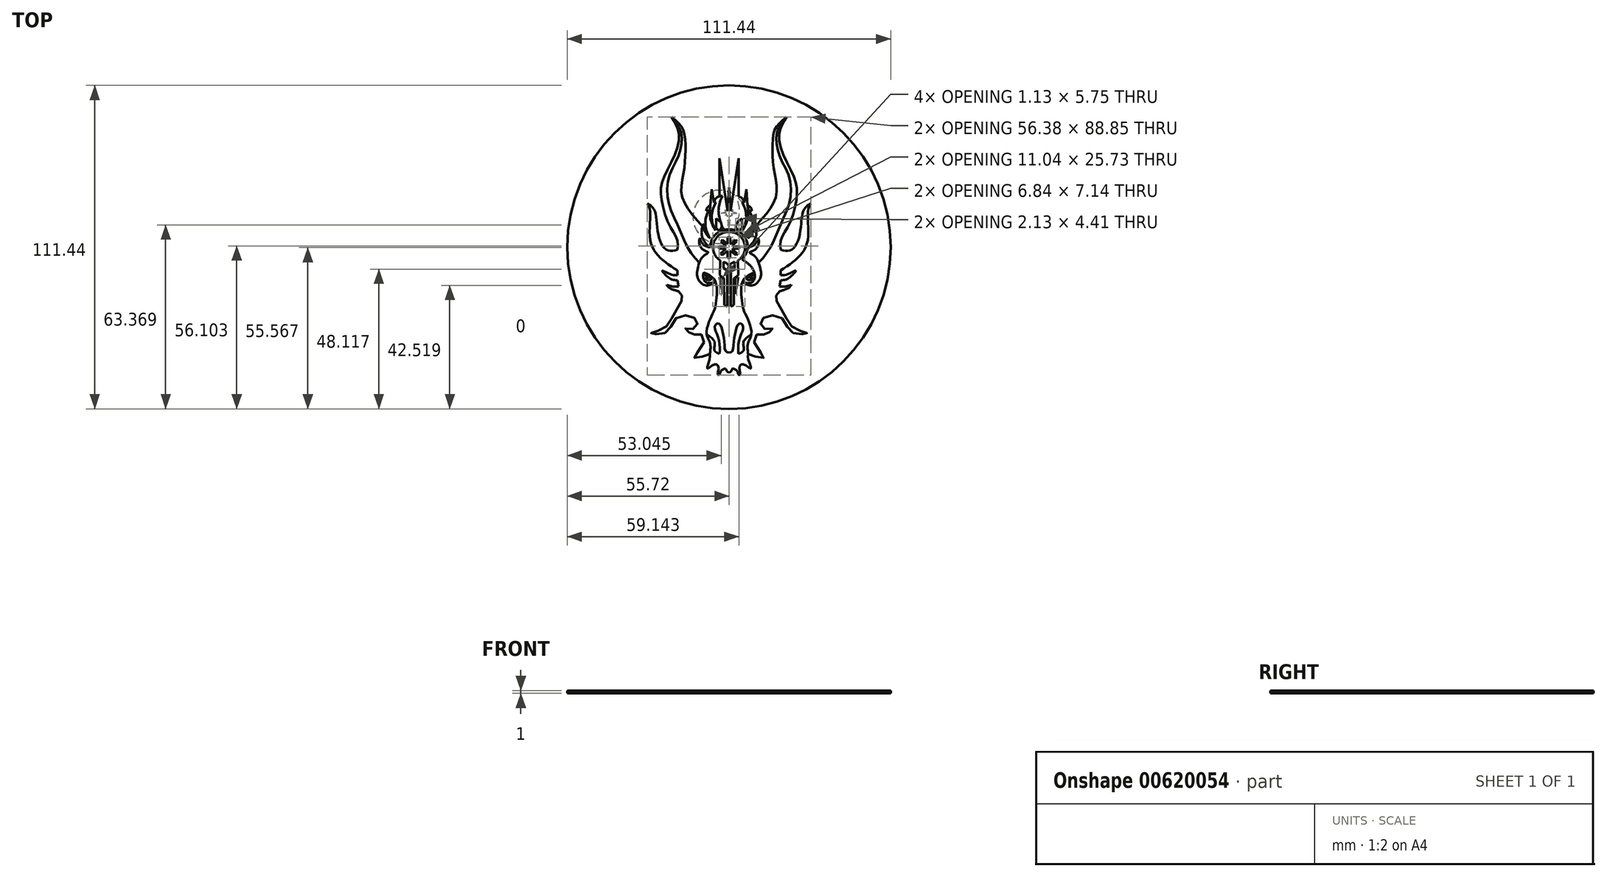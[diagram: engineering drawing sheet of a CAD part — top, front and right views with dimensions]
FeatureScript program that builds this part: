
annotation { "Feature Type Name" : "Feature", "Feature Type Description" : "" }
export const myFeature = defineFeature(function(context is Context, id is Id, definition is map)
    precondition{}
    {
        {
            var Q0;
            Q0=qCreatedBy(makeId("Top.planeOp"),FACE);
            var sketch = newSketch(context, id + "F0", { "sketchPlane" : qUnion([Q0])});
            skLineSegment(sketch, "E0", {"start": v(0.64, -20.47) * mm, "end": v(1.63, -19.96) * mm});
            skLineSegment(sketch, "E1", {"start": v(1.63, -19.96) * mm, "end": v(1.73, -10.73) * mm});
            skLineSegment(sketch, "E2", {"start": v(1.73, -10.73) * mm, "end": v(3.14, -9.62) * mm});
            skLineSegment(sketch, "E3", {"start": v(0.64, -20.47) * mm, "end": v(0.64, -8.04) * mm});
            skLineSegment(sketch, "E4", {"start": v(0.64, -8.04) * mm, "end": v(1.91, -7.17) * mm});
            skLineSegment(sketch, "E5", {"start": v(1.91, -7.17) * mm, "end": v(1.91, -5.13) * mm});
            skArc(sketch, "E6", {"start": v(0, -5.41) * mm, "mid": v(5.52, -0.08) * mm, "end": v(0, 5.26) * mm});
            skLineSegment(sketch, "E7", {"start": v(3.14, -9.62) * mm, "end": v(3.08, -4.56) * mm});
            skLineSegment(sketch, "E8", {"start": v(2.78, 8.47) * mm, "end": v(4.49, 9.86) * mm});
            skLineSegment(sketch, "E9", {"start": v(4.49, 9.86) * mm, "end": v(4.49, 6.67) * mm});
            skLineSegment(sketch, "E10", {"start": v(4.49, 6.67) * mm, "end": v(3.26, 5.44) * mm});
            skLineSegment(sketch, "E11", {"start": v(3.26, 5.44) * mm, "end": v(2.36, 7.04) * mm});
            skArc(sketch, "E12", {"start": v(2.78, 8.47) * mm, "mid": v(3.6, 13.1) * mm, "end": v(2.25, 17.62) * mm});
            skArc(sketch, "E13", {"start": v(1.4, 5.97) * mm, "mid": v(1.94, 6.45) * mm, "end": v(2.36, 7.04) * mm});
            skArc(sketch, "E14", {"start": v(5.2, 15.4) * mm, "mid": v(4.16, 17.1) * mm, "end": v(2.25, 17.62) * mm});
            skArc(sketch, "E15", {"start": v(4.66, 5.73) * mm, "mid": v(5.95, 10.6) * mm, "end": v(4.49, 15.4) * mm});
            skArc(sketch, "E16", {"start": v(4.66, 5.73) * mm, "mid": v(6.4, 9.87) * mm, "end": v(6.4, 14.36) * mm});
            skArc(sketch, "E17", {"start": v(7.87, 12.55) * mm, "mid": v(7.4, 13.67) * mm, "end": v(6.4, 14.36) * mm});
            skArc(sketch, "E18", {"start": v(6.4, 3.03) * mm, "mid": v(8.15, 7.7) * mm, "end": v(7.02, 12.55) * mm});
            skArc(sketch, "E19", {"start": v(6.4, 3.03) * mm, "mid": v(8.24, 5.24) * mm, "end": v(8.72, 8.06) * mm});
            skArc(sketch, "E20", {"start": v(6.4, 0) * mm, "mid": v(9.22, 3.55) * mm, "end": v(8.72, 8.06) * mm});
            skArc(sketch, "E21", {"start": v(6.4, 0) * mm, "mid": v(8.83, 0.88) * mm, "end": v(10, 3.17) * mm});
            skArc(sketch, "E22", {"start": v(7.87, -1.4) * mm, "mid": v(9.96, 0.4) * mm, "end": v(10, 3.17) * mm});
            skArc(sketch, "E23", {"start": v(4.4, -4.17) * mm, "mid": v(6.17, 1.87) * mm, "end": v(1.4, 5.97) * mm});
            skLineSegment(sketch, "E24", {"start": v(2.11, -11.19) * mm, "end": v(3.24, -10.33) * mm});
            skLineSegment(sketch, "E25", {"start": v(3.24, -10.33) * mm, "end": v(2.13, -16.08) * mm});
            skLineSegment(sketch, "E26", {"start": v(2.13, -16.08) * mm, "end": v(2.11, -11.19) * mm});
            skFitSpline(sketch, "E27", {"points": [v(4.4, -4.17) * mm, v(7.37, -6.41) * mm, v(8.7, -8.69) * mm, v(8.8, -10.78) * mm, v(7.79, -12.14) * mm, v(5.83, -12.33) * mm, v(4.9, -12.1) * mm], "startDerivative": vector(14.8, -9.52) * mm, "endDerivative": vector(-7.08, 2.25) * mm});
            skFitSpline(sketch, "E28", {"points": [v(4.9, -12.1) * mm, v(6.3, -12.93) * mm, v(8.86, -12.9) * mm, v(10.92, -10.27) * mm, v(10.85, -7.7) * mm, v(8.96, -3.16) * mm, v(7.15, -1.86) * mm, v(7.87, -1.4) * mm], "startDerivative": vector(10.53, -7.87) * mm, "endDerivative": vector(13.03, 5.28) * mm});
            skLineSegment(sketch, "E29", {"start": v(0, 6.49) * mm, "end": v(0.53, 10.42) * mm});
            skLineSegment(sketch, "E30", {"start": v(0.53, 10.42) * mm, "end": v(0.53, 10.9) * mm});
            skLineSegment(sketch, "E31", {"start": v(0.53, 10.9) * mm, "end": v(1.11, 10.9) * mm});
            skLineSegment(sketch, "E32", {"start": v(1.11, 10.9) * mm, "end": v(0.9, 11.5) * mm});
            skLineSegment(sketch, "E33", {"start": v(0.9, 11.5) * mm, "end": v(2.65, 11.74) * mm});
            skLineSegment(sketch, "E34", {"start": v(2.65, 11.74) * mm, "end": v(1.05, 12.22) * mm});
            skLineSegment(sketch, "E35", {"start": v(1.05, 12.22) * mm, "end": v(1.43, 12.9) * mm});
            skLineSegment(sketch, "E36", {"start": v(1.43, 12.9) * mm, "end": v(0.54, 12.51) * mm});
            skLineSegment(sketch, "E37", {"start": v(4.49, 15.4) * mm, "end": v(5.2, 15.4) * mm});
            skLineSegment(sketch, "E38", {"start": v(7.02, 12.55) * mm, "end": v(7.87, 12.55) * mm});
            skLineSegment(sketch, "E39", {"start": v(0.54, 12.51) * mm, "end": v(0, 20.62) * mm});
            skFitSpline(sketch, "E40", {"points": [v(9.1, 7.21) * mm, v(11.57, 9.94) * mm, v(16.22, 17.62) * mm, v(15.5, 26.76) * mm, v(15.04, 35.45) * mm, v(16.05, 41.02) * mm, v(19.84, 44.8) * mm], "startDerivative": vector(17.57, 18.84) * mm, "endDerivative": vector(30.07, 23.23) * mm});
            skFitSpline(sketch, "E41", {"points": [v(19.84, 44.8) * mm, v(17.95, 41.4) * mm, v(17.57, 35.2) * mm, v(22.5, 23.82) * mm, v(23.38, 17.62) * mm, v(20.86, 8.06) * mm, v(17.95, 2.86) * mm, v(17.82, -0.94) * mm], "startDerivative": vector(-19, -28.92) * mm, "endDerivative": vector(3.8, -35.47) * mm});
            skFitSpline(sketch, "E42", {"points": [v(17.82, -0.94) * mm, v(21.49, -0.94) * mm, v(24.4, 4.5) * mm, v(25.66, 12.55) * mm, v(28.2, 15) * mm], "startDerivative": vector(18.53, -4.1) * mm, "endDerivative": vector(14.4, 8.9) * mm});
            skFitSpline(sketch, "E43", {"points": [v(28.2, 15) * mm, v(27.2, 12.55) * mm, v(27.2, 2.86) * mm, v(23.9, -3.47) * mm, v(17.82, -8.02) * mm], "startDerivative": vector(-7.89, -11.91) * mm, "endDerivative": vector(-24.05, -15.72) * mm});
            skFitSpline(sketch, "E44", {"points": [v(17.82, -9.6) * mm, v(19.84, -9.45) * mm, v(22.97, -8.12) * mm, v(22.2, -9.26) * mm, v(19.84, -11.05) * mm, v(17.82, -11.4) * mm], "startDerivative": vector(9, -1.2) * mm, "endDerivative": vector(-10.69, -0.53) * mm});
            skFitSpline(sketch, "E45", {"points": [v(17.41, -13.6) * mm, v(19.43, -13.54) * mm, v(21.5, -12.99) * mm], "startDerivative": vector(4.1, -0.14) * mm, "endDerivative": vector(4.08, 1.35) * mm});
            skFitSpline(sketch, "E46", {"points": [v(21.5, -12.99) * mm, v(20.47, -14.08) * mm, v(17.41, -15.2) * mm], "startDerivative": vector(-2.04, -2.86) * mm, "endDerivative": vector(-5.9, -1.63) * mm});
            skFitSpline(sketch, "E47", {"points": [v(16.22, -16.63) * mm, v(16.22, -18.21) * mm, v(18.81, -22.8) * mm, v(21.5, -27.16) * mm, v(25.66, -29.19) * mm, v(26.89, -29.7) * mm, v(24.1, -29.98) * mm, v(20.72, -28.5) * mm, v(17.82, -24.1) * mm, v(12.47, -24.07) * mm, v(10.92, -26.03) * mm, v(11.97, -28.05) * mm, v(15, -28.05) * mm, v(14.24, -29.07) * mm, v(12.4, -30.05) * mm, v(9.88, -29.98) * mm, v(8.72, -32.93) * mm, v(12.12, -37.94) * mm, v(10.06, -37.94) * mm, v(6.57, -36.87) * mm], "startDerivative": vector(-7.73, -38) * mm, "endDerivative": vector(-58.93, 20.62) * mm});
            skFitSpline(sketch, "E48", {"points": [v(6.57, -36.87) * mm, v(6.77, -39.08) * mm, v(7.5, -41.8) * mm, v(5.91, -40.84) * mm, v(4.27, -40.38) * mm, v(3.57, -41.53) * mm, v(3.81, -42.88) * mm, v(3.8, -43.99) * mm, v(3.3, -43.97) * mm, v(2.93, -42.88) * mm, v(1.9, -41.98) * mm, v(1.1, -41.87) * mm, v(0.8, -42.7) * mm, v(0, -43.12) * mm], "startDerivative": vector(-1, -19.1) * mm, "endDerivative": vector(-15.31, -4.03) * mm});
            skFitSpline(sketch, "E49", {"points": [v(6.57, -36.87) * mm, v(6.57, -32.93) * mm, v(7.68, -30.03) * mm, v(6.57, -24.92) * mm, v(4.96, -21.32) * mm, v(4.27, -16.76) * mm, v(4.9, -11.39) * mm, v(8.7, -8.69) * mm], "startDerivative": vector(-3.54, 31.13) * mm, "endDerivative": vector(30.9, 14.24) * mm});
            skFitSpline(sketch, "E50", {"points": [v(10.23, -5.36) * mm, v(13.96, -0.61) * mm, v(17.95, 8.06) * mm, v(20.86, 15.59) * mm, v(20.86, 23.82) * mm, v(17.95, 30.25) * mm, v(16.39, 35.89) * mm, v(16.74, 40.18) * mm, v(19.84, 44.8) * mm], "startDerivative": vector(32.67, 35.42) * mm, "endDerivative": vector(33.02, 40.5) * mm});
            skFitSpline(sketch, "E51", {"points": [v(7.68, -30.03) * mm, v(4.9, -32.93) * mm, v(4.9, -35.74) * mm, v(0.8, -37.26) * mm, v(0, -37.26) * mm], "startDerivative": vector(-12.98, -8.92) * mm, "endDerivative": vector(-4.07, 0.48) * mm});
            skFitSpline(sketch, "E52", {"points": [v(3.24, -36.75) * mm, v(3.24, -33.56) * mm, v(4.27, -29.61) * mm, v(4.9, -27.84) * mm, v(4.27, -26.36) * mm, v(3.24, -26.54) * mm, v(2.25, -28.96) * mm, v(1.63, -32.93) * mm, v(1.1, -35.89) * mm, v(0, -36.33) * mm], "startDerivative": vector(-1.6, 23.43) * mm, "endDerivative": vector(-16.16, -2.15) * mm});
            skFitSpline(sketch, "E53", {"points": [v(6.16, -11.09) * mm, v(6.95, -10.16) * mm, v(8.89, -9.7) * mm, v(8.2, -10.97) * mm, v(6.16, -11.09) * mm]});
            skFitSpline(sketch, "E54", {"points": [v(6.95, -10.16) * mm, v(8.2, -10.97) * mm, v(7.93, -10.45) * mm, v(6.95, -10.16) * mm]});
            skLineSegment(sketch, "E55", {"start": v(0.54, 12.51) * mm, "end": v(3.34, 30.61) * mm});
            skLineSegment(sketch, "E56", {"start": v(3.34, 30.61) * mm, "end": v(3.34, 17.51) * mm});
            skLineSegment(sketch, "E57", {"start": v(5.2, 15.4) * mm, "end": v(5.93, 19.97) * mm});
            skLineSegment(sketch, "E58", {"start": v(5.93, 19.97) * mm, "end": v(6.4, 14.36) * mm});
            skLineSegment(sketch, "E59", {"start": v(8.72, 8.06) * mm, "end": v(8.72, 12.11) * mm});
            skArc(sketch, "E60", {"start": v(0.43, -1.43) * mm, "mid": v(0.55, -1.39) * mm, "end": v(0.66, -1.33) * mm});
            skLineSegment(sketch, "E61", {"start": v(0, 3.42) * mm, "end": v(0.45, 3.42) * mm});
            skLineSegment(sketch, "E62", {"start": v(0.45, 3.42) * mm, "end": v(0.45, 1.24) * mm});
            skLineSegment(sketch, "E63", {"start": v(0.68, 1.13) * mm, "end": v(2.25, 2.52) * mm});
            skLineSegment(sketch, "E64", {"start": v(2.25, 2.52) * mm, "end": v(2.74, 1.96) * mm});
            skLineSegment(sketch, "E65", {"start": v(2.74, 1.96) * mm, "end": v(1.2, 0.62) * mm});
            skLineSegment(sketch, "E66", {"start": v(0, -3.72) * mm, "end": v(0.43, -3.72) * mm});
            skLineSegment(sketch, "E67", {"start": v(0.43, -3.72) * mm, "end": v(0.43, -1.43) * mm});
            skLineSegment(sketch, "E68", {"start": v(0.66, -1.33) * mm, "end": v(2.38, -2.74) * mm});
            skLineSegment(sketch, "E69", {"start": v(2.38, -2.74) * mm, "end": v(2.86, -2.15) * mm});
            skLineSegment(sketch, "E70", {"start": v(2.86, -2.15) * mm, "end": v(1.2, -0.8) * mm});
            skLineSegment(sketch, "E71", {"start": v(1.33, -0.52) * mm, "end": v(3.42, -0.52) * mm});
            skLineSegment(sketch, "E72", {"start": v(3.42, -0.52) * mm, "end": v(3.42, 0.24) * mm});
            skLineSegment(sketch, "E73", {"start": v(3.42, 0.24) * mm, "end": v(1.36, 0.24) * mm});
            skArc(sketch, "E74.trimOffspring", {"start": v(1.36, 0.24) * mm, "mid": v(1.3, 0.44) * mm, "end": v(1.2, 0.62) * mm});
            skArc(sketch, "E75.trimOffspring", {"start": v(0.68, 1.13) * mm, "mid": v(0.57, 1.2) * mm, "end": v(0.45, 1.24) * mm});
            skArc(sketch, "E76.trimOffspring", {"start": v(1.2, -0.8) * mm, "mid": v(1.28, -0.66) * mm, "end": v(1.33, -0.52) * mm});
            skPoint(sketch, "E77.orphan", {"position": v(0, -1.5) * mm});
            skPoint(sketch, "E78.orphan", {"position": v(0, 1.32) * mm});
            skLineSegment(sketch, "E79", {"start": v(16.22, -16.63) * mm, "end": v(17.41, -15.2) * mm});
            skLineSegment(sketch, "E80", {"start": v(17.82, -11.4) * mm, "end": v(17.41, -13.6) * mm});
            skLineSegment(sketch, "E81", {"start": v(17.82, -8.02) * mm, "end": v(17.82, -9.6) * mm});
            skArc(sketch, "E82.MirrorCS", {"start": v(-0.68, 1.13) * mm, "mid": v(-0.57, 1.2) * mm, "end": v(-0.45, 1.24) * mm});
            skLineSegment(sketch, "E83.MirrorCS", {"start": v(-1.33, -0.52) * mm, "end": v(-3.42, -0.52) * mm});
            skArc(sketch, "E84.MirrorCS", {"start": v(-1.36, 0.24) * mm, "mid": v(-1.3, 0.44) * mm, "end": v(-1.2, 0.62) * mm});
            skLineSegment(sketch, "E85.MirrorCS", {"start": v(-0.68, 1.13) * mm, "end": v(-2.25, 2.52) * mm});
            skLineSegment(sketch, "E86.MirrorCS", {"start": v(0, -3.72) * mm, "end": v(-0.43, -3.72) * mm});
            skLineSegment(sketch, "E87.MirrorCS", {"start": v(0, 3.42) * mm, "end": v(-0.45, 3.42) * mm});
            skLineSegment(sketch, "E88.MirrorCS", {"start": v(-2.38, -2.74) * mm, "end": v(-2.86, -2.15) * mm});
            skLineSegment(sketch, "E89.MirrorCS", {"start": v(-0.66, -1.33) * mm, "end": v(-2.38, -2.74) * mm});
            skLineSegment(sketch, "E90.MirrorCS", {"start": v(-3.42, -0.52) * mm, "end": v(-3.42, 0.24) * mm});
            skLineSegment(sketch, "E91.MirrorCS", {"start": v(-2.74, 1.96) * mm, "end": v(-1.2, 0.62) * mm});
            skLineSegment(sketch, "E92.MirrorCS", {"start": v(-2.25, 2.52) * mm, "end": v(-2.74, 1.96) * mm});
            skArc(sketch, "E93.MirrorCS", {"start": v(-1.2, -0.8) * mm, "mid": v(-1.28, -0.66) * mm, "end": v(-1.33, -0.52) * mm});
            skLineSegment(sketch, "E94.MirrorCS", {"start": v(-3.42, 0.24) * mm, "end": v(-1.36, 0.24) * mm});
            skLineSegment(sketch, "E95.MirrorCS", {"start": v(-2.86, -2.15) * mm, "end": v(-1.2, -0.8) * mm});
            skLineSegment(sketch, "E96.MirrorCS", {"start": v(-0.45, 3.42) * mm, "end": v(-0.45, 1.24) * mm});
            skLineSegment(sketch, "E97.MirrorCS", {"start": v(-0.43, -3.72) * mm, "end": v(-0.43, -1.43) * mm});
            skArc(sketch, "E98.MirrorCS", {"start": v(-0.43, -1.43) * mm, "mid": v(-0.55, -1.39) * mm, "end": v(-0.66, -1.33) * mm});
            skLineSegment(sketch, "E99.MirrorCS", {"start": v(-1.11, 10.9) * mm, "end": v(-0.9, 11.5) * mm});
            skLineSegment(sketch, "E100.MirrorCS", {"start": v(-0.53, 10.9) * mm, "end": v(-1.11, 10.9) * mm});
            skArc(sketch, "E101.MirrorCS", {"start": v(-1.4, 5.97) * mm, "mid": v(-1.94, 6.45) * mm, "end": v(-2.36, 7.04) * mm});
            skLineSegment(sketch, "E102.MirrorCS", {"start": v(-0.9, 11.5) * mm, "end": v(-2.65, 11.74) * mm});
            skLineSegment(sketch, "E103.MirrorCS", {"start": v(0, 6.49) * mm, "end": v(-0.53, 10.42) * mm});
            skLineSegment(sketch, "E104.MirrorCS", {"start": v(-3.26, 5.44) * mm, "end": v(-2.36, 7.04) * mm});
            skLineSegment(sketch, "E105.MirrorCS", {"start": v(-4.49, 6.67) * mm, "end": v(-3.26, 5.44) * mm});
            skLineSegment(sketch, "E106.MirrorCS", {"start": v(-1.05, 12.22) * mm, "end": v(-1.43, 12.9) * mm});
            skLineSegment(sketch, "E107.MirrorCS", {"start": v(-4.49, 15.4) * mm, "end": v(-5.2, 15.4) * mm});
            skLineSegment(sketch, "E108.MirrorCS", {"start": v(-7.02, 12.55) * mm, "end": v(-7.87, 12.55) * mm});
            skLineSegment(sketch, "E109.MirrorCS", {"start": v(-0.53, 10.42) * mm, "end": v(-0.53, 10.9) * mm});
            skArc(sketch, "E110.MirrorCS", {"start": v(0, -5.41) * mm, "mid": v(-5.52, -0.08) * mm, "end": v(0, 5.26) * mm});
            skLineSegment(sketch, "E111.MirrorCS", {"start": v(-2.78, 8.47) * mm, "end": v(-4.49, 9.86) * mm});
            skLineSegment(sketch, "E112.MirrorCS", {"start": v(-4.49, 9.86) * mm, "end": v(-4.49, 6.67) * mm});
            skLineSegment(sketch, "E113.MirrorCS", {"start": v(-2.65, 11.74) * mm, "end": v(-1.05, 12.22) * mm});
            skArc(sketch, "E114.MirrorCS", {"start": v(-7.87, 12.55) * mm, "mid": v(-7.4, 13.67) * mm, "end": v(-6.4, 14.36) * mm});
            skArc(sketch, "E115.MirrorCS", {"start": v(-4.66, 5.73) * mm, "mid": v(-6.4, 9.87) * mm, "end": v(-6.4, 14.36) * mm});
            skArc(sketch, "E116.MirrorCS", {"start": v(-6.4, 3.03) * mm, "mid": v(-8.24, 5.24) * mm, "end": v(-8.72, 8.06) * mm});
            skArc(sketch, "E117.MirrorCS", {"start": v(-4.4, -4.17) * mm, "mid": v(-6.17, 1.87) * mm, "end": v(-1.4, 5.97) * mm});
            skFitSpline(sketch, "E118.MirrorCS", {"points": [v(-17.41, -13.6) * mm, v(-19.43, -13.54) * mm, v(-21.5, -12.99) * mm], "startDerivative": vector(-4.1, -0.14) * mm, "endDerivative": vector(-4.08, 1.35) * mm});
            skArc(sketch, "E119.MirrorCS", {"start": v(-4.66, 5.73) * mm, "mid": v(-5.95, 10.6) * mm, "end": v(-4.49, 15.4) * mm});
            skLineSegment(sketch, "E120.MirrorCS", {"start": v(-1.43, 12.9) * mm, "end": v(-0.54, 12.51) * mm});
            skLineSegment(sketch, "E121.MirrorCS", {"start": v(-2.11, -11.19) * mm, "end": v(-3.24, -10.33) * mm});
            skFitSpline(sketch, "E122.MirrorCS", {"points": [v(-4.4, -4.17) * mm, v(-7.37, -6.41) * mm, v(-8.7, -8.69) * mm, v(-8.8, -10.78) * mm, v(-7.79, -12.14) * mm, v(-5.83, -12.33) * mm, v(-4.9, -12.1) * mm], "startDerivative": vector(-14.8, -9.52) * mm, "endDerivative": vector(7.08, 2.25) * mm});
            skLineSegment(sketch, "E123.MirrorCS", {"start": v(-17.82, -8.02) * mm, "end": v(-17.82, -9.6) * mm});
            skLineSegment(sketch, "E124.MirrorCS", {"start": v(-2.13, -16.08) * mm, "end": v(-2.11, -11.19) * mm});
            skLineSegment(sketch, "E125.MirrorCS", {"start": v(-5.2, 15.4) * mm, "end": v(-5.93, 19.97) * mm});
            skLineSegment(sketch, "E126.MirrorCS", {"start": v(-8.72, 8.06) * mm, "end": v(-8.72, 12.11) * mm});
            skFitSpline(sketch, "E127.MirrorCS", {"points": [v(-4.9, -12.1) * mm, v(-6.3, -12.93) * mm, v(-8.86, -12.9) * mm, v(-10.92, -10.27) * mm, v(-10.85, -7.7) * mm, v(-8.96, -3.16) * mm, v(-7.15, -1.86) * mm, v(-7.87, -1.4) * mm], "startDerivative": vector(-10.53, -7.87) * mm, "endDerivative": vector(-13.03, 5.28) * mm});
            skArc(sketch, "E128.MirrorCS", {"start": v(-7.87, -1.4) * mm, "mid": v(-9.96, 0.4) * mm, "end": v(-10, 3.17) * mm});
            skArc(sketch, "E129.MirrorCS", {"start": v(-6.4, 3.03) * mm, "mid": v(-8.15, 7.7) * mm, "end": v(-7.02, 12.55) * mm});
            skFitSpline(sketch, "E130.MirrorC", {"points": [v(-6.16, -11.09) * mm, v(-6.95, -10.16) * mm, v(-8.89, -9.7) * mm, v(-8.2, -10.97) * mm, v(-6.16, -11.09) * mm]});
            skFitSpline(sketch, "E131.MirrorC", {"points": [v(-6.95, -10.16) * mm, v(-8.2, -10.97) * mm, v(-7.93, -10.45) * mm, v(-6.95, -10.16) * mm]});
            skArc(sketch, "E132.MirrorCS", {"start": v(-6.4, 0) * mm, "mid": v(-9.22, 3.55) * mm, "end": v(-8.72, 8.06) * mm});
            skLineSegment(sketch, "E133.MirrorCS", {"start": v(-17.82, -11.4) * mm, "end": v(-17.41, -13.6) * mm});
            skFitSpline(sketch, "E134.MirrorCS", {"points": [v(-21.5, -12.99) * mm, v(-20.47, -14.08) * mm, v(-17.41, -15.2) * mm], "startDerivative": vector(2.04, -2.86) * mm, "endDerivative": vector(5.9, -1.63) * mm});
            skLineSegment(sketch, "E135.MirrorCS", {"start": v(-0.64, -20.47) * mm, "end": v(-1.63, -19.96) * mm});
            skLineSegment(sketch, "E136.MirrorCS", {"start": v(-1.73, -10.73) * mm, "end": v(-3.14, -9.62) * mm});
            skLineSegment(sketch, "E137.MirrorCS", {"start": v(-0.64, -8.04) * mm, "end": v(-1.91, -7.17) * mm});
            skArc(sketch, "E138.MirrorCS", {"start": v(-6.4, 0) * mm, "mid": v(-8.83, 0.88) * mm, "end": v(-10, 3.17) * mm});
            skLineSegment(sketch, "E139.MirrorCS", {"start": v(-1.91, -7.17) * mm, "end": v(-1.91, -5.13) * mm});
            skLineSegment(sketch, "E140.MirrorCS", {"start": v(-3.24, -10.33) * mm, "end": v(-2.13, -16.08) * mm});
            skLineSegment(sketch, "E141.MirrorCS", {"start": v(-3.14, -9.62) * mm, "end": v(-3.08, -4.56) * mm});
            skLineSegment(sketch, "E142.MirrorCS", {"start": v(-5.93, 19.97) * mm, "end": v(-6.4, 14.36) * mm});
            skArc(sketch, "E143.MirrorCS", {"start": v(-2.78, 8.47) * mm, "mid": v(-3.6, 13.1) * mm, "end": v(-2.25, 17.62) * mm});
            skLineSegment(sketch, "E144.MirrorCS", {"start": v(-16.22, -16.63) * mm, "end": v(-17.41, -15.2) * mm});
            skFitSpline(sketch, "E145.MirrorCS", {"points": [v(-17.82, -9.6) * mm, v(-19.84, -9.45) * mm, v(-22.97, -8.12) * mm, v(-22.2, -9.26) * mm, v(-19.84, -11.05) * mm, v(-17.82, -11.4) * mm], "startDerivative": vector(-9, -1.2) * mm, "endDerivative": vector(10.69, -0.53) * mm});
            skArc(sketch, "E146.MirrorCS", {"start": v(-5.2, 15.4) * mm, "mid": v(-4.16, 17.1) * mm, "end": v(-2.25, 17.62) * mm});
            skLineSegment(sketch, "E147.MirrorCS", {"start": v(-1.63, -19.96) * mm, "end": v(-1.73, -10.73) * mm});
            skLineSegment(sketch, "E148.MirrorCS", {"start": v(-0.64, -20.47) * mm, "end": v(-0.64, -8.04) * mm});
            skFitSpline(sketch, "E149.MirrorCS", {"points": [v(-7.68, -30.03) * mm, v(-4.9, -32.93) * mm, v(-4.9, -35.74) * mm, v(-0.8, -37.26) * mm, v(0, -37.26) * mm], "startDerivative": vector(12.98, -8.92) * mm, "endDerivative": vector(4.07, 0.48) * mm});
            skFitSpline(sketch, "E150.MirrorCS", {"points": [v(-3.24, -36.75) * mm, v(-3.24, -33.56) * mm, v(-4.27, -29.61) * mm, v(-4.9, -27.84) * mm, v(-4.27, -26.36) * mm, v(-3.24, -26.54) * mm, v(-2.25, -28.96) * mm, v(-1.63, -32.93) * mm, v(-1.1, -35.89) * mm, v(0, -36.33) * mm], "startDerivative": vector(1.6, 23.43) * mm, "endDerivative": vector(16.16, -2.15) * mm});
            skFitSpline(sketch, "E151.MirrorCS", {"points": [v(-6.57, -36.87) * mm, v(-6.77, -39.08) * mm, v(-7.5, -41.8) * mm, v(-5.91, -40.84) * mm, v(-4.27, -40.38) * mm, v(-3.57, -41.53) * mm, v(-3.81, -42.88) * mm, v(-3.8, -43.99) * mm, v(-3.3, -43.97) * mm, v(-2.93, -42.88) * mm, v(-1.9, -41.98) * mm, v(-1.1, -41.87) * mm, v(-0.8, -42.7) * mm, v(0, -43.12) * mm], "startDerivative": vector(1, -19.1) * mm, "endDerivative": vector(15.31, -4.03) * mm});
            skLineSegment(sketch, "E152.MirrorCS", {"start": v(-0.54, 12.51) * mm, "end": v(0, 20.62) * mm});
            skFitSpline(sketch, "E153.MirrorCS", {"points": [v(-6.57, -36.87) * mm, v(-6.57, -32.93) * mm, v(-7.68, -30.03) * mm, v(-6.57, -24.92) * mm, v(-4.96, -21.32) * mm, v(-4.27, -16.76) * mm, v(-4.9, -11.39) * mm, v(-8.7, -8.69) * mm], "startDerivative": vector(3.54, 31.13) * mm, "endDerivative": vector(-30.9, 14.24) * mm});
            skLineSegment(sketch, "E154.MirrorCS", {"start": v(-3.34, 30.61) * mm, "end": v(-3.34, 17.51) * mm});
            skLineSegment(sketch, "E155.MirrorCS", {"start": v(-0.54, 12.51) * mm, "end": v(-3.34, 30.61) * mm});
            skFitSpline(sketch, "E156.MirrorCS", {"points": [v(-17.82, -0.94) * mm, v(-21.49, -0.94) * mm, v(-24.4, 4.5) * mm, v(-25.66, 12.55) * mm, v(-28.2, 15) * mm], "startDerivative": vector(-18.53, -4.1) * mm, "endDerivative": vector(-14.4, 8.9) * mm});
            skFitSpline(sketch, "E157.MirrorCS", {"points": [v(-19.84, 44.8) * mm, v(-17.95, 41.4) * mm, v(-17.57, 35.2) * mm, v(-22.5, 23.82) * mm, v(-23.38, 17.62) * mm, v(-20.86, 8.06) * mm, v(-17.95, 2.86) * mm, v(-17.82, -0.94) * mm], "startDerivative": vector(19, -28.92) * mm, "endDerivative": vector(-3.8, -35.47) * mm});
            skFitSpline(sketch, "E158.MirrorCS", {"points": [v(-10.23, -5.36) * mm, v(-13.96, -0.61) * mm, v(-17.95, 8.06) * mm, v(-20.86, 15.59) * mm, v(-20.86, 23.82) * mm, v(-17.95, 30.25) * mm, v(-16.39, 35.89) * mm, v(-16.74, 40.18) * mm, v(-19.84, 44.8) * mm], "startDerivative": vector(-32.67, 35.42) * mm, "endDerivative": vector(-33.02, 40.5) * mm});
            skFitSpline(sketch, "E159.MirrorCS", {"points": [v(-28.2, 15) * mm, v(-27.2, 12.55) * mm, v(-27.2, 2.86) * mm, v(-23.9, -3.47) * mm, v(-17.82, -8.02) * mm], "startDerivative": vector(7.89, -11.91) * mm, "endDerivative": vector(24.05, -15.72) * mm});
            skFitSpline(sketch, "E160.MirrorCS", {"points": [v(-16.22, -16.63) * mm, v(-16.22, -18.21) * mm, v(-18.81, -22.8) * mm, v(-21.5, -27.16) * mm, v(-25.66, -29.19) * mm, v(-26.89, -29.7) * mm, v(-24.1, -29.98) * mm, v(-20.72, -28.5) * mm, v(-17.82, -24.1) * mm, v(-12.47, -24.07) * mm, v(-10.92, -26.03) * mm, v(-11.97, -28.05) * mm, v(-15, -28.05) * mm, v(-14.24, -29.07) * mm, v(-12.4, -30.05) * mm, v(-9.88, -29.98) * mm, v(-8.72, -32.93) * mm, v(-12.12, -37.94) * mm, v(-10.06, -37.94) * mm, v(-6.57, -36.87) * mm], "startDerivative": vector(7.73, -38) * mm, "endDerivative": vector(58.93, 20.62) * mm});
            skFitSpline(sketch, "E161.MirrorCS", {"points": [v(-9.1, 7.21) * mm, v(-11.57, 9.94) * mm, v(-16.22, 17.62) * mm, v(-15.5, 26.76) * mm, v(-15.04, 35.45) * mm, v(-16.05, 41.02) * mm, v(-19.84, 44.8) * mm], "startDerivative": vector(-17.57, 18.84) * mm, "endDerivative": vector(-30.07, 23.23) * mm});
            skLineSegment(sketch, "E162", {"start": v(2.36, 7.04) * mm, "end": v(2.78, 8.47) * mm});
            skLineSegment(sketch, "E163", {"start": v(-2.36, 7.04) * mm, "end": v(-2.78, 8.47) * mm});
            skCircle(sketch, "E164", {"center": v(0, 0) * mm, "radius": 55.72 * mm});
            skArc(sketch, "E165", {"start": v(1.4, 5.97) * mm, "mid": v(0, 6.16) * mm, "end": v(-1.4, 5.97) * mm});
            skArc(sketch, "E166", {"start": v(-4.4, -4.17) * mm, "mid": v(0, -5.87) * mm, "end": v(4.4, -4.17) * mm});
            skLineSegment(sketch, "E167", {"start": v(-0.64, -20.47) * mm, "end": v(0.64, -20.47) * mm});
            skArc(sketch, "E168", {"start": v(0, -7.05) * mm, "mid": v(-0.62, -5.76) * mm, "end": v(-1.91, -5.13) * mm});
            skPoint(sketch, "E168.startSnap0", {"position": v(0, -5.87) * mm});
            skArc(sketch, "E169.MirrorCS", {"start": v(0, -7.05) * mm, "mid": v(0.62, -5.76) * mm, "end": v(1.91, -5.13) * mm});
            skSolve(sketch);
        }
        {
            var Q0;
            Q0=makeQuery(id+"F0.imprint","IMPRINT",FACE,{"disambiguationData":[TD([[makeQuery(id+"F0.imprint","IMPRINT",EDGE,{"derivedFrom":sQuery(id+"F0.wireOp",EDGE,"E41")}),-1.0]])]});
            var Q1;
            Q1=makeQuery(id+"F0.imprint","IMPRINT",FACE,{"disambiguationData":[TD([[makeQuery(id+"F0.imprint","IMPRINT",EDGE,{"derivedFrom":sQuery(id+"F0.wireOp",EDGE,"E118.MirrorCS")}),1.0]])]});
            var Q2;
            {var subQ0=sQuery(id+"F0.wireOp",EDGE,"E54");var subQ1=sQuery(id+"F0.wireOp",EDGE,"E53");var subQ2=makeQuery(id+"F0.imprint","INTERSECT",VERTEX,{"disambiguationData":[OD(0.0)],"derivedFrom":[subQ1,subQ0]});Q2=makeQuery(id+"F0.imprint","IMPRINT",FACE,{"disambiguationData":[TD([[makeQuery(id+"F0.imprint","IMPRINT",EDGE,{"disambiguationData":[TD([[subQ2,1.0]])],"derivedFrom":subQ1}),-1.0]])]});}
            var Q3;
            {var subQ0=sQuery(id+"F0.wireOp",EDGE,"E131.MirrorC");var subQ1=sQuery(id+"F0.wireOp",EDGE,"E130.MirrorC");var subQ2=makeQuery(id+"F0.imprint","INTERSECT",VERTEX,{"disambiguationData":[OD(0.0)],"derivedFrom":[subQ1,subQ0]});Q3=makeQuery(id+"F0.imprint","IMPRINT",FACE,{"disambiguationData":[TD([[makeQuery(id+"F0.imprint","IMPRINT",EDGE,{"disambiguationData":[TD([[subQ2,1.0]])],"derivedFrom":subQ1}),1.0]])]});}
            var Q4;
            Q4=makeQuery(id+"F0.imprint","IMPRINT",FACE,{"disambiguationData":[TD([[makeQuery(id+"F0.imprint","IMPRINT",EDGE,{"derivedFrom":sQuery(id+"F0.wireOp",EDGE,"E60")}),1.0]])]});
            var Q5;
            Q5=makeQuery(id+"F0.imprint","IMPRINT",FACE,{"disambiguationData":[TD([[makeQuery(id+"F0.imprint","IMPRINT",EDGE,{"derivedFrom":sQuery(id+"F0.wireOp",EDGE,"E8")}),-1.0]])]});
            var Q6;
            Q6=makeQuery(id+"F0.imprint","IMPRINT",FACE,{"disambiguationData":[TD([[makeQuery(id+"F0.imprint","IMPRINT",EDGE,{"derivedFrom":sQuery(id+"F0.wireOp",EDGE,"E104.MirrorCS")}),1.0]])]});
            extrude(context, id + "F1", {"entities" : qUnion([Q0, Q1, Q2, Q3, Q4, Q5, Q6]), "depth" : .2 * mm, "offsetDistance" : 25.4 * mm});
        }
        {
            var Q0;
            {var subQ4=sQuery(id+"F0.wireOp",EDGE,"E48");Q0=makeQuery(id+"F0.imprint","IMPRINT",FACE,{"disambiguationData":[TD([[makeQuery(id+"F0.imprint","IMPRINT",EDGE,{"derivedFrom":subQ4}),-1.0]])]});}
            var Q1;
            {var subQ3=sQuery(id+"F0.wireOp",EDGE,"E52");Q1=makeQuery(id+"F0.imprint","IMPRINT",FACE,{"disambiguationData":[TD([[makeQuery(id+"F0.imprint","IMPRINT",EDGE,{"derivedFrom":subQ3}),1.0]])]});}
            extrude(context, id + "F2", {"entities" : qUnion([Q0, Q1]), "depth" : .2 * mm, "offsetDistance" : 25.4 * mm});
        }
        {
            var Q0;
            {var subQ3=sQuery(id+"F0.wireOp",EDGE,"E21");Q0=makeQuery(id+"F0.imprint","IMPRINT",FACE,{"disambiguationData":[TD([[makeQuery(id+"F0.imprint","IMPRINT",EDGE,{"derivedFrom":subQ3}),1.0]])]});}
            var Q1;
            {var subQ3=sQuery(id+"F0.wireOp",EDGE,"E128.MirrorCS");Q1=makeQuery(id+"F0.imprint","IMPRINT",FACE,{"disambiguationData":[TD([[makeQuery(id+"F0.imprint","IMPRINT",EDGE,{"derivedFrom":subQ3}),1.0]])]});}
            var Q2;
            Q2=makeQuery(id+"F0.imprint","IMPRINT",FACE,{"disambiguationData":[TD([[makeQuery(id+"F0.imprint","IMPRINT",EDGE,{"derivedFrom":sQuery(id+"F0.wireOp",EDGE,"E107.MirrorCS")}),1.0]])]});
            var Q3;
            Q3=makeQuery(id+"F0.imprint","IMPRINT",FACE,{"disambiguationData":[TD([[makeQuery(id+"F0.imprint","IMPRINT",EDGE,{"derivedFrom":sQuery(id+"F0.wireOp",EDGE,"E15")}),-1.0]])]});
            var Q4;
            {var subQ1=sQuery(id+"F0.wireOp",EDGE,"E12");Q4=makeQuery(id+"F0.imprint","IMPRINT",FACE,{"disambiguationData":[TD([[makeQuery(id+"F0.imprint","IMPRINT",EDGE,{"derivedFrom":subQ1}),1.0]])]});}
            var Q5;
            {var subQ7=sQuery(id+"F0.wireOp",EDGE,"E165");Q5=makeQuery(id+"F0.imprint","IMPRINT",FACE,{"disambiguationData":[TD([[makeQuery(id+"F0.imprint","IMPRINT",EDGE,{"derivedFrom":subQ7}),1.0]])]});}
            var Q6;
            Q6=makeQuery(id+"F0.imprint","IMPRINT",FACE,{"disambiguationData":[TD([[makeQuery(id+"F0.imprint","IMPRINT",EDGE,{"derivedFrom":sQuery(id+"F0.wireOp",EDGE,"E0")}),-1.0]])]});
            var Q7;
            Q7=makeQuery(id+"F0.imprint","IMPRINT",FACE,{"disambiguationData":[TD([[makeQuery(id+"F0.imprint","IMPRINT",EDGE,{"derivedFrom":sQuery(id+"F0.wireOp",EDGE,"E3")}),1.0]])]});
            var Q8;
            {var subQ2=sQuery(id+"F0.wireOp",EDGE,"E5");var subQ4=sQuery(id+"F0.wireOp",EDGE,"E166");var subQ5=makeQuery(id+"F0.imprint","INTERSECT",VERTEX,{"derivedFrom":[subQ2,subQ4]});Q8=makeQuery(id+"F0.imprint","IMPRINT",FACE,{"disambiguationData":[TD([[makeQuery(id+"F0.imprint","IMPRINT",EDGE,{"disambiguationData":[TD([[subQ5,1.0]])],"derivedFrom":subQ4}),1.0]])]});}
            var Q9;
            {var subQ1=sQuery(id+"F0.wireOp",EDGE,"E139.MirrorCS");var subQ5=sQuery(id+"F0.wireOp",EDGE,"E166");var subQ6=makeQuery(id+"F0.imprint","INTERSECT",VERTEX,{"derivedFrom":[subQ1,subQ5]});Q9=makeQuery(id+"F0.imprint","IMPRINT",FACE,{"disambiguationData":[TD([[makeQuery(id+"F0.imprint","IMPRINT",EDGE,{"disambiguationData":[TD([[subQ6,-1.0]])],"derivedFrom":subQ5}),1.0]])]});}
            extrude(context, id + "F3", {"entities" : qUnion([Q0, Q1, Q2, Q3, Q4, Q5, Q6, Q7, Q8, Q9]), "depth" : .3 * mm, "offsetDistance" : 25.4 * mm});
        }
        {
            var Q0;
            Q0=makeQuery(id+"F0.imprint","IMPRINT",FACE,{"disambiguationData":[TD([[makeQuery(id+"F0.imprint","IMPRINT",EDGE,{"derivedFrom":sQuery(id+"F0.wireOp",EDGE,"E60")}),-1.0]])]});
            var Q1;
            {var subQ11=sQuery(id+"F0.wireOp",EDGE,"E128.MirrorCS");Q1=makeQuery(id+"F0.imprint","IMPRINT",FACE,{"disambiguationData":[TD([[makeQuery(id+"F0.imprint","IMPRINT",EDGE,{"derivedFrom":subQ11}),-1.0]])]});}
            var Q2;
            {var subQ4=sQuery(id+"F0.wireOp",EDGE,"E101.MirrorCS");Q2=makeQuery(id+"F0.imprint","IMPRINT",FACE,{"disambiguationData":[TD([[makeQuery(id+"F0.imprint","IMPRINT",EDGE,{"derivedFrom":subQ4}),1.0]])]});}
            var Q3;
            Q3=makeQuery(id+"F0.imprint","IMPRINT",FACE,{"disambiguationData":[TD([[makeQuery(id+"F0.imprint","IMPRINT",EDGE,{"derivedFrom":sQuery(id+"F0.wireOp",EDGE,"E8")}),1.0]])]});
            var Q4;
            {var subQ4=sQuery(id+"F0.wireOp",EDGE,"E21");Q4=makeQuery(id+"F0.imprint","IMPRINT",FACE,{"disambiguationData":[TD([[makeQuery(id+"F0.imprint","IMPRINT",EDGE,{"derivedFrom":subQ4}),-1.0]])]});}
            var Q5;
            Q5=makeQuery(id+"F0.imprint","IMPRINT",FACE,{"disambiguationData":[TD([[makeQuery(id+"F0.imprint","IMPRINT",EDGE,{"derivedFrom":sQuery(id+"F0.wireOp",EDGE,"E0")}),1.0]])]});
            var Q6;
            Q6=makeQuery(id+"F0.imprint","IMPRINT",FACE,{"disambiguationData":[TD([[makeQuery(id+"F0.imprint","IMPRINT",EDGE,{"derivedFrom":sQuery(id+"F0.wireOp",EDGE,"E135.MirrorCS")}),-1.0]])]});
            var Q7;
            Q7=makeQuery(id+"F0.imprint","IMPRINT",FACE,{"disambiguationData":[TD([[makeQuery(id+"F0.imprint","IMPRINT",EDGE,{"derivedFrom":sQuery(id+"F0.wireOp",EDGE,"E121.MirrorCS")}),1.0]])]});
            var Q8;
            Q8=makeQuery(id+"F0.imprint","IMPRINT",FACE,{"disambiguationData":[TD([[makeQuery(id+"F0.imprint","IMPRINT",EDGE,{"derivedFrom":sQuery(id+"F0.wireOp",EDGE,"E24")}),-1.0]])]});
            var Q9;
            {var subQ1=sQuery(id+"F0.wireOp",EDGE,"E6");var subQ3=sQuery(id+"F0.wireOp",EDGE,"E110.MirrorCS");var subQ4=makeQuery(id+"F0.imprint","INTERSECT",VERTEX,{"disambiguationData":[OD(0.0)],"derivedFrom":[subQ1,subQ3]});Q9=makeQuery(id+"F0.imprint","IMPRINT",FACE,{"disambiguationData":[TD([[makeQuery(id+"F0.imprint","IMPRINT",EDGE,{"disambiguationData":[TD([[subQ4,-1.0]])],"derivedFrom":subQ1}),-1.0]])]});}
            var Q10;
            Q10=makeQuery(id+"F0.imprint","IMPRINT",FACE,{"disambiguationData":[TD([[makeQuery(id+"F0.imprint","IMPRINT",EDGE,{"derivedFrom":sQuery(id+"F0.wireOp",EDGE,"E29")}),1.0]])]});
            var Q11;
            {var subQ1=sQuery(id+"F0.wireOp",EDGE,"E110.MirrorCS");var subQ3=sQuery(id+"F0.wireOp",EDGE,"E141.MirrorCS");var subQ4=makeQuery(id+"F0.imprint","INTERSECT",VERTEX,{"derivedFrom":[subQ1,subQ3]});Q11=makeQuery(id+"F0.imprint","IMPRINT",FACE,{"disambiguationData":[TD([[makeQuery(id+"F0.imprint","IMPRINT",EDGE,{"disambiguationData":[TD([[subQ4,1.0]])],"derivedFrom":subQ3}),-1.0]])]});}
            var Q12;
            {var subQ0=sQuery(id+"F0.wireOp",EDGE,"E6");var subQ5=sQuery(id+"F0.wireOp",EDGE,"E7");var subQ6=makeQuery(id+"F0.imprint","INTERSECT",VERTEX,{"derivedFrom":[subQ0,subQ5]});Q12=makeQuery(id+"F0.imprint","IMPRINT",FACE,{"disambiguationData":[TD([[makeQuery(id+"F0.imprint","IMPRINT",EDGE,{"disambiguationData":[TD([[subQ6,1.0]])],"derivedFrom":subQ5}),1.0]])]});}
            var Q13;
            {var subQ0=sQuery(id+"F0.wireOp",EDGE,"E877.MirrorCS");var subQ1=sQuery(id+"F0.wireOp",EDGE,"5gOgUQ9P-rn9S-5wVc-aoTu-rHQglzzc4Tzq");var subQ2=makeQuery(id+"F0.imprint","INTERSECT",VERTEX,{"disambiguationData":[OD(1.0)],"derivedFrom":[subQ1,subQ0]});Q13=makeQuery(id+"F0.imprint","IMPRINT",FACE,{"disambiguationData":[TD([[makeQuery(id+"F0.imprint","IMPRINT",EDGE,{"disambiguationData":[TD([[subQ2,1.0]])],"derivedFrom":subQ1}),-1.0]])]});}
            var Q14;
            {var subQ0=sQuery(id+"F0.wireOp",EDGE,"E168");var subQ1=sQuery(id+"F0.wireOp",EDGE,"E166");var subQ2=makeQuery(id+"F0.imprint","INTERSECT",VERTEX,{"derivedFrom":[subQ1,subQ0]});Q14=makeQuery(id+"F0.imprint","IMPRINT",FACE,{"disambiguationData":[TD([[makeQuery(id+"F0.imprint","IMPRINT",EDGE,{"disambiguationData":[TD([[subQ2,-1.0]])],"derivedFrom":subQ1}),-1.0]])]});}
            extrude(context, id + "F4", {"entities" : qUnion([Q0, Q1, Q2, Q3, Q4, Q5, Q6, Q7, Q8, Q9, Q10, Q11, Q12, Q13, Q14]), "depth" : .4 * mm, "offsetDistance" : 25.4 * mm});
        }
        {
            var Q0;
            Q0=makeQuery(id+"F0.imprint","IMPRINT",FACE,{"disambiguationData":[TD([[makeQuery(id+"F0.imprint","IMPRINT",EDGE,{"derivedFrom":sQuery(id+"F0.wireOp",EDGE,"E17")}),-1.0]])]});
            var Q1;
            {var subQ0=sQuery(id+"F0.wireOp",EDGE,"E131.MirrorC");var subQ1=sQuery(id+"F0.wireOp",EDGE,"E130.MirrorC");var subQ2=makeQuery(id+"F0.imprint","INTERSECT",VERTEX,{"disambiguationData":[OD(1.0)],"derivedFrom":[subQ1,subQ0]});Q1=makeQuery(id+"F0.imprint","IMPRINT",FACE,{"disambiguationData":[TD([[makeQuery(id+"F0.imprint","IMPRINT",EDGE,{"disambiguationData":[TD([[subQ2,1.0]])],"derivedFrom":subQ1}),1.0]])]});}
            var Q2;
            {var subQ0=sQuery(id+"F0.wireOp",EDGE,"E54");var subQ1=sQuery(id+"F0.wireOp",EDGE,"E53");var subQ2=makeQuery(id+"F0.imprint","INTERSECT",VERTEX,{"disambiguationData":[OD(1.0)],"derivedFrom":[subQ1,subQ0]});Q2=makeQuery(id+"F0.imprint","IMPRINT",FACE,{"disambiguationData":[TD([[makeQuery(id+"F0.imprint","IMPRINT",EDGE,{"disambiguationData":[TD([[subQ2,1.0]])],"derivedFrom":subQ1}),-1.0]])]});}
            var Q3;
            {var subQ0=sQuery(id+"F0.wireOp",EDGE,"E53");var subQ1=sQuery(id+"F0.wireOp",EDGE,"E27");var subQ2=makeQuery(id+"F0.imprint","INTERSECT",VERTEX,{"disambiguationData":[OD(0.0)],"derivedFrom":[subQ1,subQ0]});Q3=makeQuery(id+"F0.imprint","IMPRINT",FACE,{"disambiguationData":[TD([[makeQuery(id+"F0.imprint","IMPRINT",EDGE,{"disambiguationData":[TD([[subQ2,-1.0]])],"derivedFrom":subQ1}),-1.0]])]});}
            var Q4;
            {var subQ0=sQuery(id+"F0.wireOp",EDGE,"E130.MirrorC");var subQ1=sQuery(id+"F0.wireOp",EDGE,"E122.MirrorCS");var subQ2=makeQuery(id+"F0.imprint","INTERSECT",VERTEX,{"disambiguationData":[OD(0.0)],"derivedFrom":[subQ1,subQ0]});Q4=makeQuery(id+"F0.imprint","IMPRINT",FACE,{"disambiguationData":[TD([[makeQuery(id+"F0.imprint","IMPRINT",EDGE,{"disambiguationData":[TD([[subQ2,-1.0]])],"derivedFrom":subQ1}),1.0]])]});}
            extrude(context, id + "F5", {"entities" : qUnion([Q0, Q1, Q2, Q3, Q4]), "depth" : .5 * mm, "offsetDistance" : 25.4 * mm});
        }
        {
            var Q0;
            Q0=sQuery(id+"F0.wireOp",EDGE,"E164");
            extrude(context, id + "F6", {"bodyType" : ToolBodyType.SURFACE, "surfaceEntities" : qUnion([Q0]), "depth" : .4 * mm, "offsetDistance" : 25.4 * mm});
        }
        {
            var Q0;
            Q0=makeQuery(id+"F5.opExtrude","SWEPT_BODY",BODY,{"disambiguationData":[OSD([sQuery(id+"F0.wireOp",EDGE,"E14"),sQuery(id+"F0.wireOp",EDGE,"E17"),sQuery(id+"F0.wireOp",EDGE,"E18"),sQuery(id+"F0.wireOp",EDGE,"E19"),sQuery(id+"F0.wireOp",EDGE,"E20"),sQuery(id+"F0.wireOp",EDGE,"E38"),sQuery(id+"F0.wireOp",EDGE,"E39"),sQuery(id+"F0.wireOp",EDGE,"E40"),sQuery(id+"F0.wireOp",EDGE,"E41"),sQuery(id+"F0.wireOp",EDGE,"E42"),sQuery(id+"F0.wireOp",EDGE,"E43"),sQuery(id+"F0.wireOp",EDGE,"E44"),sQuery(id+"F0.wireOp",EDGE,"E45"),sQuery(id+"F0.wireOp",EDGE,"E46"),sQuery(id+"F0.wireOp",EDGE,"E47"),sQuery(id+"F0.wireOp",EDGE,"E48"),sQuery(id+"F0.wireOp",EDGE,"E55"),sQuery(id+"F0.wireOp",EDGE,"E56"),sQuery(id+"F0.wireOp",EDGE,"E57"),sQuery(id+"F0.wireOp",EDGE,"E58"),sQuery(id+"F0.wireOp",EDGE,"E79"),sQuery(id+"F0.wireOp",EDGE,"E80"),sQuery(id+"F0.wireOp",EDGE,"E81"),sQuery(id+"F0.wireOp",EDGE,"E108.MirrorCS"),sQuery(id+"F0.wireOp",EDGE,"E114.MirrorCS"),sQuery(id+"F0.wireOp",EDGE,"E116.MirrorCS"),sQuery(id+"F0.wireOp",EDGE,"E118.MirrorCS"),sQuery(id+"F0.wireOp",EDGE,"E123.MirrorCS"),sQuery(id+"F0.wireOp",EDGE,"E125.MirrorCS"),sQuery(id+"F0.wireOp",EDGE,"E129.MirrorCS"),sQuery(id+"F0.wireOp",EDGE,"E132.MirrorCS"),sQuery(id+"F0.wireOp",EDGE,"E133.MirrorCS"),sQuery(id+"F0.wireOp",EDGE,"E134.MirrorCS"),sQuery(id+"F0.wireOp",EDGE,"E142.MirrorCS"),sQuery(id+"F0.wireOp",EDGE,"E144.MirrorCS"),sQuery(id+"F0.wireOp",EDGE,"E145.MirrorCS"),sQuery(id+"F0.wireOp",EDGE,"E146.MirrorCS"),sQuery(id+"F0.wireOp",EDGE,"E151.MirrorCS"),sQuery(id+"F0.wireOp",EDGE,"E152.MirrorCS"),sQuery(id+"F0.wireOp",EDGE,"E154.MirrorCS"),sQuery(id+"F0.wireOp",EDGE,"E155.MirrorCS"),sQuery(id+"F0.wireOp",EDGE,"E156.MirrorCS"),sQuery(id+"F0.wireOp",EDGE,"E157.MirrorCS"),sQuery(id+"F0.wireOp",EDGE,"E159.MirrorCS"),sQuery(id+"F0.wireOp",EDGE,"E160.MirrorCS"),sQuery(id+"F0.wireOp",EDGE,"E161.MirrorCS"),sQuery(id+"F0.wireOp",EDGE,"E164")])]});
            var Q1;
            Q1=makeQuery(id+"F6.opExtrude","SWEPT_BODY",BODY,{"disambiguationData":[OSD([sQuery(id+"F0.wireOp",EDGE,"E164")])]});
            var Q2;
            Q2=makeQuery(id+"F4.opExtrude","SWEPT_BODY",BODY,{"disambiguationData":[OSD([sQuery(id+"F0.wireOp",EDGE,"E21"),sQuery(id+"F0.wireOp",EDGE,"E22"),sQuery(id+"F0.wireOp",EDGE,"E23"),sQuery(id+"F0.wireOp",EDGE,"E27"),sQuery(id+"F0.wireOp",EDGE,"E28"),sQuery(id+"F0.wireOp",EDGE,"E53")])]});
            var Q3;
            Q3=makeQuery(id+"F1.opExtrude","SWEPT_BODY",BODY,{"disambiguationData":[OSD([sQuery(id+"F0.wireOp",EDGE,"E27"),sQuery(id+"F0.wireOp",EDGE,"E28"),sQuery(id+"F0.wireOp",EDGE,"E41"),sQuery(id+"F0.wireOp",EDGE,"E42"),sQuery(id+"F0.wireOp",EDGE,"E43"),sQuery(id+"F0.wireOp",EDGE,"E44"),sQuery(id+"F0.wireOp",EDGE,"E45"),sQuery(id+"F0.wireOp",EDGE,"E46"),sQuery(id+"F0.wireOp",EDGE,"E47"),sQuery(id+"F0.wireOp",EDGE,"E49"),sQuery(id+"F0.wireOp",EDGE,"E50"),sQuery(id+"F0.wireOp",EDGE,"E53"),sQuery(id+"F0.wireOp",EDGE,"E54"),sQuery(id+"F0.wireOp",EDGE,"E79"),sQuery(id+"F0.wireOp",EDGE,"E80"),sQuery(id+"F0.wireOp",EDGE,"E81")])]});
            var Q4;
            Q4=makeQuery(id+"F2.opExtrude","SWEPT_BODY",BODY,{"disambiguationData":[OSD([sQuery(id+"F0.wireOp",EDGE,"E48"),sQuery(id+"F0.wireOp",EDGE,"E49"),sQuery(id+"F0.wireOp",EDGE,"E51"),sQuery(id+"F0.wireOp",EDGE,"E52"),sQuery(id+"F0.wireOp",EDGE,"E149.MirrorCS"),sQuery(id+"F0.wireOp",EDGE,"E150.MirrorCS"),sQuery(id+"F0.wireOp",EDGE,"E151.MirrorCS"),sQuery(id+"F0.wireOp",EDGE,"E153.MirrorCS")])]});
            var Q5;
            Q5=makeQuery(id+"F3.opExtrude","SWEPT_BODY",BODY,{"disambiguationData":[OSD([sQuery(id+"F0.wireOp",EDGE,"E20"),sQuery(id+"F0.wireOp",EDGE,"E21"),sQuery(id+"F0.wireOp",EDGE,"E22"),sQuery(id+"F0.wireOp",EDGE,"E28"),sQuery(id+"F0.wireOp",EDGE,"E40"),sQuery(id+"F0.wireOp",EDGE,"E50")])]});
            var Q6;
            Q6=makeQuery(id+"F3.opExtrude","SWEPT_BODY",BODY,{"disambiguationData":[OSD([sQuery(id+"F0.wireOp",EDGE,"E0"),sQuery(id+"F0.wireOp",EDGE,"E1"),sQuery(id+"F0.wireOp",EDGE,"E2"),sQuery(id+"F0.wireOp",EDGE,"E3"),sQuery(id+"F0.wireOp",EDGE,"E4"),sQuery(id+"F0.wireOp",EDGE,"E5"),sQuery(id+"F0.wireOp",EDGE,"E6"),sQuery(id+"F0.wireOp",EDGE,"E7"),sQuery(id+"F0.wireOp",EDGE,"E12"),sQuery(id+"F0.wireOp",EDGE,"E13"),sQuery(id+"F0.wireOp",EDGE,"E14"),sQuery(id+"F0.wireOp",EDGE,"E23"),sQuery(id+"F0.wireOp",EDGE,"E24"),sQuery(id+"F0.wireOp",EDGE,"E25"),sQuery(id+"F0.wireOp",EDGE,"E26"),sQuery(id+"F0.wireOp",EDGE,"E27"),sQuery(id+"F0.wireOp",EDGE,"E29"),sQuery(id+"F0.wireOp",EDGE,"E30"),sQuery(id+"F0.wireOp",EDGE,"E31"),sQuery(id+"F0.wireOp",EDGE,"E32"),sQuery(id+"F0.wireOp",EDGE,"E33"),sQuery(id+"F0.wireOp",EDGE,"E34"),sQuery(id+"F0.wireOp",EDGE,"E35"),sQuery(id+"F0.wireOp",EDGE,"E36"),sQuery(id+"F0.wireOp",EDGE,"E49"),sQuery(id+"F0.wireOp",EDGE,"E51"),sQuery(id+"F0.wireOp",EDGE,"E52"),sQuery(id+"F0.wireOp",EDGE,"E55"),sQuery(id+"F0.wireOp",EDGE,"E56"),sQuery(id+"F0.wireOp",EDGE,"E99.MirrorCS"),sQuery(id+"F0.wireOp",EDGE,"E100.MirrorCS"),sQuery(id+"F0.wireOp",EDGE,"E101.MirrorCS"),sQuery(id+"F0.wireOp",EDGE,"E102.MirrorCS"),sQuery(id+"F0.wireOp",EDGE,"E103.MirrorCS"),sQuery(id+"F0.wireOp",EDGE,"E106.MirrorCS"),sQuery(id+"F0.wireOp",EDGE,"E109.MirrorCS"),sQuery(id+"F0.wireOp",EDGE,"E110.MirrorCS"),sQuery(id+"F0.wireOp",EDGE,"E113.MirrorCS"),sQuery(id+"F0.wireOp",EDGE,"E117.MirrorCS"),sQuery(id+"F0.wireOp",EDGE,"E120.MirrorCS"),sQuery(id+"F0.wireOp",EDGE,"E121.MirrorCS"),sQuery(id+"F0.wireOp",EDGE,"E122.MirrorCS"),sQuery(id+"F0.wireOp",EDGE,"E124.MirrorCS"),sQuery(id+"F0.wireOp",EDGE,"E135.MirrorCS"),sQuery(id+"F0.wireOp",EDGE,"E136.MirrorCS"),sQuery(id+"F0.wireOp",EDGE,"E137.MirrorCS"),sQuery(id+"F0.wireOp",EDGE,"E139.MirrorCS"),sQuery(id+"F0.wireOp",EDGE,"E140.MirrorCS"),sQuery(id+"F0.wireOp",EDGE,"E141.MirrorCS"),sQuery(id+"F0.wireOp",EDGE,"E143.MirrorCS"),sQuery(id+"F0.wireOp",EDGE,"E146.MirrorCS"),sQuery(id+"F0.wireOp",EDGE,"E147.MirrorCS"),sQuery(id+"F0.wireOp",EDGE,"E148.MirrorCS"),sQuery(id+"F0.wireOp",EDGE,"E149.MirrorCS"),sQuery(id+"F0.wireOp",EDGE,"E150.MirrorCS"),sQuery(id+"F0.wireOp",EDGE,"E153.MirrorCS"),sQuery(id+"F0.wireOp",EDGE,"E154.MirrorCS"),sQuery(id+"F0.wireOp",EDGE,"E155.MirrorCS"),sQuery(id+"F0.wireOp",EDGE,"E162"),sQuery(id+"F0.wireOp",EDGE,"E163"),sQuery(id+"F0.wireOp",EDGE,"E168"),sQuery(id+"F0.wireOp",EDGE,"E169.MirrorCS")])]});
            var Q7;
            Q7=makeQuery(id+"F1.opExtrude","SWEPT_BODY",BODY,{"disambiguationData":[OSD([sQuery(id+"F0.wireOp",EDGE,"E60"),sQuery(id+"F0.wireOp",EDGE,"E61"),sQuery(id+"F0.wireOp",EDGE,"E62"),sQuery(id+"F0.wireOp",EDGE,"E63"),sQuery(id+"F0.wireOp",EDGE,"E64"),sQuery(id+"F0.wireOp",EDGE,"E65"),sQuery(id+"F0.wireOp",EDGE,"E66"),sQuery(id+"F0.wireOp",EDGE,"E67"),sQuery(id+"F0.wireOp",EDGE,"E68"),sQuery(id+"F0.wireOp",EDGE,"E69"),sQuery(id+"F0.wireOp",EDGE,"E70"),sQuery(id+"F0.wireOp",EDGE,"E71"),sQuery(id+"F0.wireOp",EDGE,"E72"),sQuery(id+"F0.wireOp",EDGE,"E73"),sQuery(id+"F0.wireOp",EDGE,"E74.trimOffspring"),sQuery(id+"F0.wireOp",EDGE,"E75.trimOffspring"),sQuery(id+"F0.wireOp",EDGE,"E76.trimOffspring"),sQuery(id+"F0.wireOp",EDGE,"E82.MirrorCS"),sQuery(id+"F0.wireOp",EDGE,"E83.MirrorCS"),sQuery(id+"F0.wireOp",EDGE,"E84.MirrorCS"),sQuery(id+"F0.wireOp",EDGE,"E85.MirrorCS"),sQuery(id+"F0.wireOp",EDGE,"E86.MirrorCS"),sQuery(id+"F0.wireOp",EDGE,"E87.MirrorCS"),sQuery(id+"F0.wireOp",EDGE,"E88.MirrorCS"),sQuery(id+"F0.wireOp",EDGE,"E89.MirrorCS"),sQuery(id+"F0.wireOp",EDGE,"E90.MirrorCS"),sQuery(id+"F0.wireOp",EDGE,"E91.MirrorCS"),sQuery(id+"F0.wireOp",EDGE,"E92.MirrorCS"),sQuery(id+"F0.wireOp",EDGE,"E93.MirrorCS"),sQuery(id+"F0.wireOp",EDGE,"E94.MirrorCS"),sQuery(id+"F0.wireOp",EDGE,"E95.MirrorCS"),sQuery(id+"F0.wireOp",EDGE,"E96.MirrorCS"),sQuery(id+"F0.wireOp",EDGE,"E97.MirrorCS"),sQuery(id+"F0.wireOp",EDGE,"E98.MirrorCS")])]});
            var Q8;
            Q8=makeQuery(id+"F4.opExtrude","SWEPT_BODY",BODY,{"disambiguationData":[OSD([sQuery(id+"F0.wireOp",EDGE,"E0"),sQuery(id+"F0.wireOp",EDGE,"E1"),sQuery(id+"F0.wireOp",EDGE,"E2"),sQuery(id+"F0.wireOp",EDGE,"E3"),sQuery(id+"F0.wireOp",EDGE,"E4"),sQuery(id+"F0.wireOp",EDGE,"E5"),sQuery(id+"F0.wireOp",EDGE,"E6"),sQuery(id+"F0.wireOp",EDGE,"E7"),sQuery(id+"F0.wireOp",EDGE,"E60"),sQuery(id+"F0.wireOp",EDGE,"E61"),sQuery(id+"F0.wireOp",EDGE,"E62"),sQuery(id+"F0.wireOp",EDGE,"E63"),sQuery(id+"F0.wireOp",EDGE,"E64"),sQuery(id+"F0.wireOp",EDGE,"E65"),sQuery(id+"F0.wireOp",EDGE,"E66"),sQuery(id+"F0.wireOp",EDGE,"E67"),sQuery(id+"F0.wireOp",EDGE,"E68"),sQuery(id+"F0.wireOp",EDGE,"E69"),sQuery(id+"F0.wireOp",EDGE,"E70"),sQuery(id+"F0.wireOp",EDGE,"E71"),sQuery(id+"F0.wireOp",EDGE,"E72"),sQuery(id+"F0.wireOp",EDGE,"E73"),sQuery(id+"F0.wireOp",EDGE,"E74.trimOffspring"),sQuery(id+"F0.wireOp",EDGE,"E75.trimOffspring"),sQuery(id+"F0.wireOp",EDGE,"E76.trimOffspring"),sQuery(id+"F0.wireOp",EDGE,"E82.MirrorCS"),sQuery(id+"F0.wireOp",EDGE,"E83.MirrorCS"),sQuery(id+"F0.wireOp",EDGE,"E84.MirrorCS"),sQuery(id+"F0.wireOp",EDGE,"E85.MirrorCS"),sQuery(id+"F0.wireOp",EDGE,"E86.MirrorCS"),sQuery(id+"F0.wireOp",EDGE,"E87.MirrorCS"),sQuery(id+"F0.wireOp",EDGE,"E88.MirrorCS"),sQuery(id+"F0.wireOp",EDGE,"E89.MirrorCS"),sQuery(id+"F0.wireOp",EDGE,"E90.MirrorCS"),sQuery(id+"F0.wireOp",EDGE,"E91.MirrorCS"),sQuery(id+"F0.wireOp",EDGE,"E92.MirrorCS"),sQuery(id+"F0.wireOp",EDGE,"E93.MirrorCS"),sQuery(id+"F0.wireOp",EDGE,"E94.MirrorCS"),sQuery(id+"F0.wireOp",EDGE,"E95.MirrorCS"),sQuery(id+"F0.wireOp",EDGE,"E96.MirrorCS"),sQuery(id+"F0.wireOp",EDGE,"E97.MirrorCS"),sQuery(id+"F0.wireOp",EDGE,"E98.MirrorCS"),sQuery(id+"F0.wireOp",EDGE,"E110.MirrorCS"),sQuery(id+"F0.wireOp",EDGE,"E135.MirrorCS"),sQuery(id+"F0.wireOp",EDGE,"E136.MirrorCS"),sQuery(id+"F0.wireOp",EDGE,"E137.MirrorCS"),sQuery(id+"F0.wireOp",EDGE,"E139.MirrorCS"),sQuery(id+"F0.wireOp",EDGE,"E141.MirrorCS"),sQuery(id+"F0.wireOp",EDGE,"E147.MirrorCS"),sQuery(id+"F0.wireOp",EDGE,"E148.MirrorCS"),sQuery(id+"F0.wireOp",EDGE,"E168"),sQuery(id+"F0.wireOp",EDGE,"E169.MirrorCS")])]});
            var Q9;
            Q9=makeQuery(id+"F1.opExtrude","SWEPT_BODY",BODY,{"disambiguationData":[OSD([sQuery(id+"F0.wireOp",EDGE,"E118.MirrorCS"),sQuery(id+"F0.wireOp",EDGE,"E122.MirrorCS"),sQuery(id+"F0.wireOp",EDGE,"E123.MirrorCS"),sQuery(id+"F0.wireOp",EDGE,"E127.MirrorCS"),sQuery(id+"F0.wireOp",EDGE,"E130.MirrorC"),sQuery(id+"F0.wireOp",EDGE,"E131.MirrorC"),sQuery(id+"F0.wireOp",EDGE,"E133.MirrorCS"),sQuery(id+"F0.wireOp",EDGE,"E134.MirrorCS"),sQuery(id+"F0.wireOp",EDGE,"E144.MirrorCS"),sQuery(id+"F0.wireOp",EDGE,"E145.MirrorCS"),sQuery(id+"F0.wireOp",EDGE,"E153.MirrorCS"),sQuery(id+"F0.wireOp",EDGE,"E156.MirrorCS"),sQuery(id+"F0.wireOp",EDGE,"E157.MirrorCS"),sQuery(id+"F0.wireOp",EDGE,"E158.MirrorCS"),sQuery(id+"F0.wireOp",EDGE,"E159.MirrorCS"),sQuery(id+"F0.wireOp",EDGE,"E160.MirrorCS")])]});
            var Q10;
            Q10=makeQuery(id+"F4.opExtrude","SWEPT_BODY",BODY,{"disambiguationData":[OSD([sQuery(id+"F0.wireOp",EDGE,"E8"),sQuery(id+"F0.wireOp",EDGE,"E9"),sQuery(id+"F0.wireOp",EDGE,"E10"),sQuery(id+"F0.wireOp",EDGE,"E11"),sQuery(id+"F0.wireOp",EDGE,"E12"),sQuery(id+"F0.wireOp",EDGE,"E13"),sQuery(id+"F0.wireOp",EDGE,"E14"),sQuery(id+"F0.wireOp",EDGE,"E15"),sQuery(id+"F0.wireOp",EDGE,"E16"),sQuery(id+"F0.wireOp",EDGE,"E17"),sQuery(id+"F0.wireOp",EDGE,"E18"),sQuery(id+"F0.wireOp",EDGE,"E19"),sQuery(id+"F0.wireOp",EDGE,"E20"),sQuery(id+"F0.wireOp",EDGE,"E23"),sQuery(id+"F0.wireOp",EDGE,"E37"),sQuery(id+"F0.wireOp",EDGE,"E38")])]});
            var Q11;
            Q11=makeQuery(id+"F4.opExtrude","SWEPT_BODY",BODY,{"disambiguationData":[OSD([sQuery(id+"F0.wireOp",EDGE,"E24"),sQuery(id+"F0.wireOp",EDGE,"E25"),sQuery(id+"F0.wireOp",EDGE,"E26")])]});
            var Q12;
            Q12=makeQuery(id+"F3.opExtrude","SWEPT_BODY",BODY,{"disambiguationData":[OSD([sQuery(id+"F0.wireOp",EDGE,"E15"),sQuery(id+"F0.wireOp",EDGE,"E16"),sQuery(id+"F0.wireOp",EDGE,"E37"),sQuery(id+"F0.wireOp",EDGE,"E57"),sQuery(id+"F0.wireOp",EDGE,"E58")])]});
            var Q13;
            Q13=makeQuery(id+"F3.opExtrude","SWEPT_BODY",BODY,{"disambiguationData":[OSD([sQuery(id+"F0.wireOp",EDGE,"E127.MirrorCS"),sQuery(id+"F0.wireOp",EDGE,"E128.MirrorCS"),sQuery(id+"F0.wireOp",EDGE,"E132.MirrorCS"),sQuery(id+"F0.wireOp",EDGE,"E138.MirrorCS"),sQuery(id+"F0.wireOp",EDGE,"E158.MirrorCS"),sQuery(id+"F0.wireOp",EDGE,"E161.MirrorCS")])]});
            var Q14;
            Q14=makeQuery(id+"F5.opExtrude","SWEPT_BODY",BODY,{"disambiguationData":[OSD([sQuery(id+"F0.wireOp",EDGE,"E27"),sQuery(id+"F0.wireOp",EDGE,"E53"),sQuery(id+"F0.wireOp",EDGE,"E54")])]});
            var Q15;
            Q15=makeQuery(id+"F4.opExtrude","SWEPT_BODY",BODY,{"disambiguationData":[OSD([sQuery(id+"F0.wireOp",EDGE,"E29"),sQuery(id+"F0.wireOp",EDGE,"E30"),sQuery(id+"F0.wireOp",EDGE,"E31"),sQuery(id+"F0.wireOp",EDGE,"E32"),sQuery(id+"F0.wireOp",EDGE,"E33"),sQuery(id+"F0.wireOp",EDGE,"E34"),sQuery(id+"F0.wireOp",EDGE,"E35"),sQuery(id+"F0.wireOp",EDGE,"E36"),sQuery(id+"F0.wireOp",EDGE,"E39"),sQuery(id+"F0.wireOp",EDGE,"E99.MirrorCS"),sQuery(id+"F0.wireOp",EDGE,"E100.MirrorCS"),sQuery(id+"F0.wireOp",EDGE,"E102.MirrorCS"),sQuery(id+"F0.wireOp",EDGE,"E103.MirrorCS"),sQuery(id+"F0.wireOp",EDGE,"E106.MirrorCS"),sQuery(id+"F0.wireOp",EDGE,"E109.MirrorCS"),sQuery(id+"F0.wireOp",EDGE,"E113.MirrorCS"),sQuery(id+"F0.wireOp",EDGE,"E120.MirrorCS"),sQuery(id+"F0.wireOp",EDGE,"E152.MirrorCS")])]});
            var Q16;
            Q16=makeQuery(id+"F1.opExtrude","SWEPT_BODY",BODY,{"disambiguationData":[OSD([sQuery(id+"F0.wireOp",EDGE,"E53"),sQuery(id+"F0.wireOp",EDGE,"E54")])]});
            var Q17;
            Q17=makeQuery(id+"F1.opExtrude","SWEPT_BODY",BODY,{"disambiguationData":[OSD([sQuery(id+"F0.wireOp",EDGE,"E8"),sQuery(id+"F0.wireOp",EDGE,"E9"),sQuery(id+"F0.wireOp",EDGE,"E10"),sQuery(id+"F0.wireOp",EDGE,"E11"),sQuery(id+"F0.wireOp",EDGE,"E162")])]});
            var Q18;
            Q18=makeQuery(id+"F3.opExtrude","SWEPT_BODY",BODY,{"disambiguationData":[OSD([sQuery(id+"F0.wireOp",EDGE,"E107.MirrorCS"),sQuery(id+"F0.wireOp",EDGE,"E115.MirrorCS"),sQuery(id+"F0.wireOp",EDGE,"E119.MirrorCS"),sQuery(id+"F0.wireOp",EDGE,"E125.MirrorCS"),sQuery(id+"F0.wireOp",EDGE,"E142.MirrorCS")])]});
            var Q19;
            Q19=makeQuery(id+"F4.opExtrude","SWEPT_BODY",BODY,{"disambiguationData":[OSD([sQuery(id+"F0.wireOp",EDGE,"E101.MirrorCS"),sQuery(id+"F0.wireOp",EDGE,"E104.MirrorCS"),sQuery(id+"F0.wireOp",EDGE,"E105.MirrorCS"),sQuery(id+"F0.wireOp",EDGE,"E107.MirrorCS"),sQuery(id+"F0.wireOp",EDGE,"E108.MirrorCS"),sQuery(id+"F0.wireOp",EDGE,"E111.MirrorCS"),sQuery(id+"F0.wireOp",EDGE,"E112.MirrorCS"),sQuery(id+"F0.wireOp",EDGE,"E114.MirrorCS"),sQuery(id+"F0.wireOp",EDGE,"E115.MirrorCS"),sQuery(id+"F0.wireOp",EDGE,"E116.MirrorCS"),sQuery(id+"F0.wireOp",EDGE,"E117.MirrorCS"),sQuery(id+"F0.wireOp",EDGE,"E119.MirrorCS"),sQuery(id+"F0.wireOp",EDGE,"E129.MirrorCS"),sQuery(id+"F0.wireOp",EDGE,"E132.MirrorCS"),sQuery(id+"F0.wireOp",EDGE,"E143.MirrorCS"),sQuery(id+"F0.wireOp",EDGE,"E146.MirrorCS")])]});
            var Q20;
            Q20=makeQuery(id+"F4.opExtrude","SWEPT_BODY",BODY,{"disambiguationData":[OSD([sQuery(id+"F0.wireOp",EDGE,"E121.MirrorCS"),sQuery(id+"F0.wireOp",EDGE,"E124.MirrorCS"),sQuery(id+"F0.wireOp",EDGE,"E140.MirrorCS")])]});
            var Q21;
            Q21=makeQuery(id+"F1.opExtrude","SWEPT_BODY",BODY,{"disambiguationData":[OSD([sQuery(id+"F0.wireOp",EDGE,"E104.MirrorCS"),sQuery(id+"F0.wireOp",EDGE,"E105.MirrorCS"),sQuery(id+"F0.wireOp",EDGE,"E111.MirrorCS"),sQuery(id+"F0.wireOp",EDGE,"E112.MirrorCS"),sQuery(id+"F0.wireOp",EDGE,"E163")])]});
            var Q22;
            Q22=makeQuery(id+"F4.opExtrude","SWEPT_BODY",BODY,{"disambiguationData":[OSD([sQuery(id+"F0.wireOp",EDGE,"E117.MirrorCS"),sQuery(id+"F0.wireOp",EDGE,"E122.MirrorCS"),sQuery(id+"F0.wireOp",EDGE,"E127.MirrorCS"),sQuery(id+"F0.wireOp",EDGE,"E128.MirrorCS"),sQuery(id+"F0.wireOp",EDGE,"E130.MirrorC"),sQuery(id+"F0.wireOp",EDGE,"E138.MirrorCS")])]});
            var Q23;
            Q23=makeQuery(id+"F5.opExtrude","SWEPT_BODY",BODY,{"disambiguationData":[OSD([sQuery(id+"F0.wireOp",EDGE,"E53"),sQuery(id+"F0.wireOp",EDGE,"E54")])]});
            var Q24;
            Q24=makeQuery(id+"F1.opExtrude","SWEPT_BODY",BODY,{"disambiguationData":[OSD([sQuery(id+"F0.wireOp",EDGE,"E130.MirrorC"),sQuery(id+"F0.wireOp",EDGE,"E131.MirrorC")])]});
            var Q25;
            Q25=makeQuery(id+"F5.opExtrude","SWEPT_BODY",BODY,{"disambiguationData":[OSD([sQuery(id+"F0.wireOp",EDGE,"E122.MirrorCS"),sQuery(id+"F0.wireOp",EDGE,"E130.MirrorC"),sQuery(id+"F0.wireOp",EDGE,"E131.MirrorC")])]});
            var Q26;
            Q26=makeQuery(id+"F5.opExtrude","SWEPT_BODY",BODY,{"disambiguationData":[OSD([sQuery(id+"F0.wireOp",EDGE,"E130.MirrorC"),sQuery(id+"F0.wireOp",EDGE,"E131.MirrorC")])]});
            var Q27;
            Q27=qCreatedBy(makeId("Top.planeOp"),FACE);
            mirror(context, id + "F7", {"entities" : qUnion([Q0, Q1, Q2, Q3, Q4, Q5, Q6, Q7, Q8, Q9, Q10, Q11, Q12, Q13, Q14, Q15, Q16, Q17, Q18, Q19, Q20, Q21, Q22, Q23, Q24, Q25, Q26]), "mirrorPlane" : qUnion([Q27])});
        }
    });
